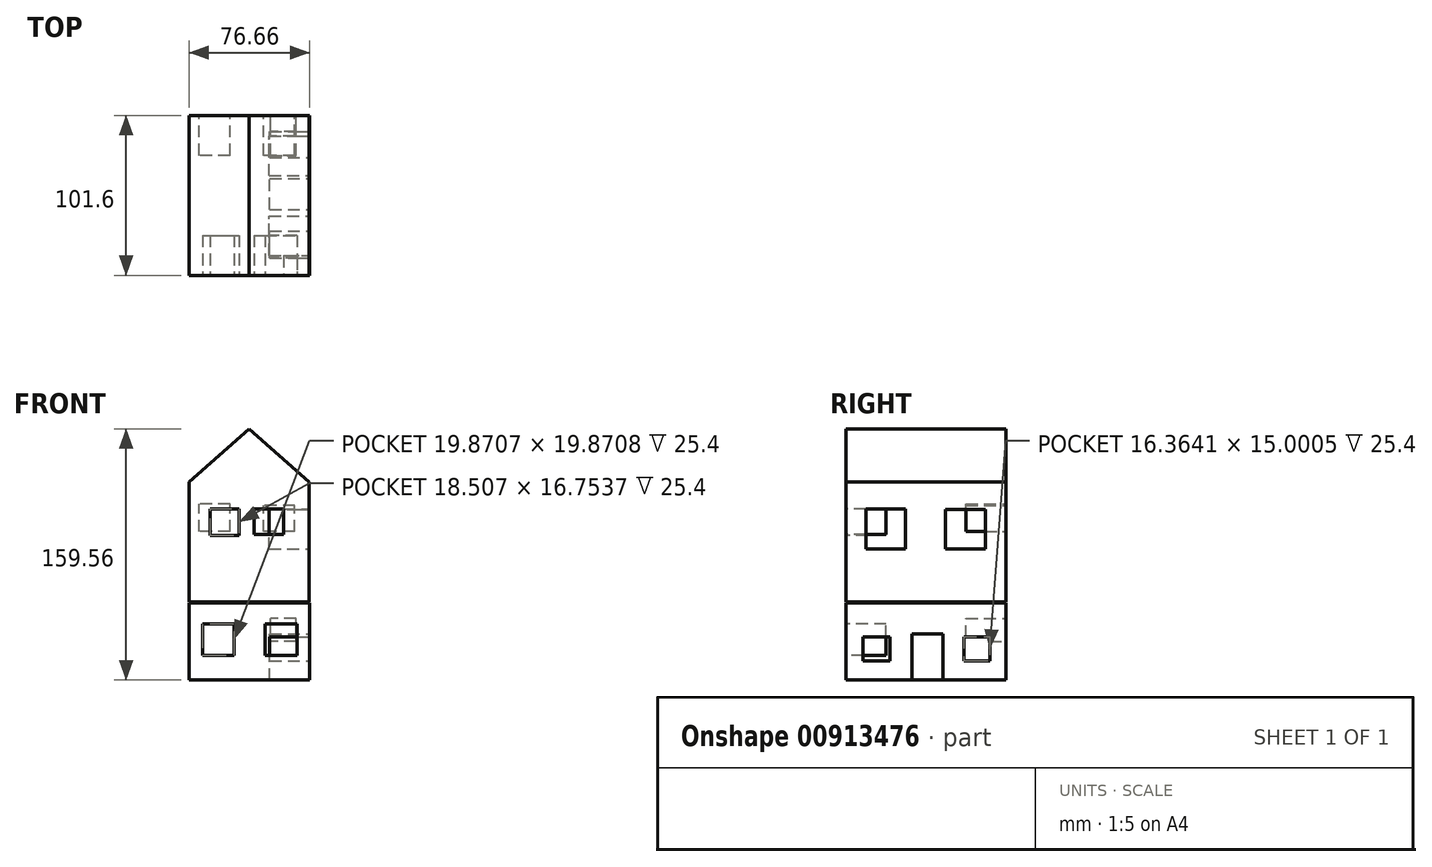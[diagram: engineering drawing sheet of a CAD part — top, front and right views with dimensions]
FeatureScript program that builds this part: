
annotation { "Feature Type Name" : "Feature", "Feature Type Description" : "" }
export const myFeature = defineFeature(function(context is Context, id is Id, definition is map)
    precondition{}
    {
        {
            var Q0;
            Q0=qCreatedBy(makeId("Front.planeOp"),FACE);
            var sketch = newSketch(context, id + "F0", { "sketchPlane" : qUnion([Q0])});
            skLineSegment(sketch, "E0.bottom", {"start": v(-63.36, 87.02) * mm, "end": v(63.64, 87.02) * mm});
            skLineSegment(sketch, "E0.top", {"start": v(-63.36, -39.98) * mm, "end": v(63.64, -39.98) * mm});
            skLineSegment(sketch, "E0.left", {"start": v(-63.36, 87.02) * mm, "end": v(-63.36, -39.98) * mm});
            skLineSegment(sketch, "E0.right", {"start": v(63.64, 87.02) * mm, "end": v(63.64, -39.98) * mm});
            skSolve(sketch);
        }
        {
            var Q0;
            Q0=makeQuery(id+"F0.imprint","IMPRINT",FACE,{"disambiguationData":[TD([[makeQuery(id+"F0.imprint","IMPRINT",EDGE,{"derivedFrom":sQuery(id+"F0.wireOp",EDGE,"E0.bottom")}),-1.0]])]});
            extrude(context, id + "F1", {"entities" : qUnion([Q0]), "depth" : 127 * mm, "offsetDistance" : 25.4 * mm});
        }
        {
            var Q0;
            Q0=makeQuery(id+"F1.opExtrude","CAP_FACE",FACE,{"disambiguationData":[OSD([sQuery(id+"F0.wireOp",EDGE,"E0.bottom"),sQuery(id+"F0.wireOp",EDGE,"E0.top"),sQuery(id+"F0.wireOp",EDGE,"E0.left"),sQuery(id+"F0.wireOp",EDGE,"E0.right")])],"isStart":false});
            extrude(context, id + "F2", {"entities" : qUnion([Q0]), "operationType" : NewBodyOperationType.ADD, "depth" : 76.2 * mm, "offsetDistance" : 25.4 * mm});
        }
        {
            var Q0;
            Q0=makeQuery(id+"F1.opExtrude","SWEPT_BODY",BODY,{"disambiguationData":[OSD([sQuery(id+"F0.wireOp",EDGE,"E0.bottom"),sQuery(id+"F0.wireOp",EDGE,"E0.top"),sQuery(id+"F0.wireOp",EDGE,"E0.left"),sQuery(id+"F0.wireOp",EDGE,"E0.right")])]});
            deleteBodies(context, id + "F3", {"entities" : qUnion([Q0])});
        }
        {
            var Q0;
            Q0=qCreatedBy(makeId("Front.planeOp"),FACE);
            var sketch = newSketch(context, id + "F4", { "sketchPlane" : qUnion([Q0])});
            skLineSegment(sketch, "E1.bottom", {"start": v(-37, 46.06) * mm, "end": v(39.2, 46.06) * mm});
            skLineSegment(sketch, "E1.top", {"start": v(-37, -30.14) * mm, "end": v(39.2, -30.14) * mm});
            skLineSegment(sketch, "E1.left", {"start": v(-37, 46.06) * mm, "end": v(-37, -30.14) * mm});
            skLineSegment(sketch, "E1.right", {"start": v(39.2, 46.06) * mm, "end": v(39.2, -30.14) * mm});
            skSolve(sketch);
        }
        {
            var Q0;
            Q0=makeQuery(id+"F4.imprint","IMPRINT",FACE,{"disambiguationData":[TD([[makeQuery(id+"F4.imprint","IMPRINT",EDGE,{"derivedFrom":sQuery(id+"F4.wireOp",EDGE,"E1.bottom")}),-1.0]])]});
            extrude(context, id + "F5", {"entities" : qUnion([Q0]), "depth" : 76.2 * mm, "offsetDistance" : 25.4 * mm});
        }
        {
            var Q0;
            Q0=makeQuery(id+"F5.opExtrude","SWEPT_BODY",BODY,{"disambiguationData":[OSD([sQuery(id+"F4.wireOp",EDGE,"E1.bottom"),sQuery(id+"F4.wireOp",EDGE,"E1.top"),sQuery(id+"F4.wireOp",EDGE,"E1.left"),sQuery(id+"F4.wireOp",EDGE,"E1.right")])]});
            deleteBodies(context, id + "F6", {"entities" : qUnion([Q0])});
        }
        {
            var Q0;
            Q0=qCreatedBy(makeId("Front.planeOp"),FACE);
            var sketch = newSketch(context, id + "F7", { "sketchPlane" : qUnion([Q0])});
            skLineSegment(sketch, "E2.bottom", {"start": v(-38.1, 42.82) * mm, "end": v(38.1, 42.82) * mm});
            skLineSegment(sketch, "E2.top", {"start": v(-38.1, -33.38) * mm, "end": v(38.1, -33.38) * mm});
            skLineSegment(sketch, "E2.left", {"start": v(-38.1, 42.82) * mm, "end": v(-38.1, -33.38) * mm});
            skLineSegment(sketch, "E2.right", {"start": v(38.1, 42.82) * mm, "end": v(38.1, -33.38) * mm});
            skLineSegment(sketch, "E3", {"start": v(-38.1, 42.82) * mm, "end": v(0, 76.42) * mm});
            skLineSegment(sketch, "E4", {"start": v(38.1, 42.82) * mm, "end": v(0, 76.42) * mm});
            skSolve(sketch);
        }
        {
            var Q0;
            Q0=makeQuery(id+"F7.imprint","IMPRINT",FACE,{"disambiguationData":[TD([[makeQuery(id+"F7.imprint","IMPRINT",EDGE,{"derivedFrom":sQuery(id+"F7.wireOp",EDGE,"E2.bottom")}),1.0]])]});
            var Q1;
            Q1=makeQuery(id+"F7.imprint","IMPRINT",FACE,{"disambiguationData":[TD([[makeQuery(id+"F7.imprint","IMPRINT",EDGE,{"derivedFrom":sQuery(id+"F7.wireOp",EDGE,"E2.bottom")}),-1.0]])]});
            extrude(context, id + "F8", {"entities" : qUnion([Q0, Q1]), "depth" : 101.6 * mm, "offsetDistance" : 25.4 * mm});
        }
        {
            var Q0;
            Q0=qCreatedBy(makeId("Front.planeOp"),FACE);
            var sketch = newSketch(context, id + "F9", { "sketchPlane" : qUnion([Q0])});
            skLineSegment(sketch, "E5.bottom", {"start": v(-38.17, -34.04) * mm, "end": v(38.5, -34.04) * mm});
            skLineSegment(sketch, "E5.top", {"start": v(-38.17, -83.14) * mm, "end": v(38.5, -83.14) * mm});
            skLineSegment(sketch, "E5.left", {"start": v(-38.17, -34.04) * mm, "end": v(-38.17, -83.14) * mm});
            skLineSegment(sketch, "E5.right", {"start": v(38.5, -34.04) * mm, "end": v(38.5, -83.14) * mm});
            skSolve(sketch);
        }
        {
            var Q0;
            Q0 = qSketchRegion(id + "F9", true);
            extrude(context, id + "F10", {"entities" : qUnion([Q0]), "depth" : 101.6 * mm, "offsetDistance" : 25.4 * mm});
        }
        {
            var Q0;
            Q0=makeQuery(id+"F10.opExtrude","SWEPT_FACE",FACE,{"disambiguationData":[OSD([sQuery(id+"F9.wireOp",EDGE,"E5.right")])]});
            var sketch = newSketch(context, id + "F11", { "sketchPlane" : qUnion([Q0])});
            skLineSegment(sketch, "E6", {"start": v(-59.66, -83.14) * mm, "end": v(-59.66, -53.82) * mm});
            skLineSegment(sketch, "E7", {"start": v(-59.66, -53.82) * mm, "end": v(-39.98, -53.82) * mm});
            skLineSegment(sketch, "E8", {"start": v(-39.98, -53.82) * mm, "end": v(-39.98, -83.14) * mm});
            skSolve(sketch);
        }
        {
            var Q0;
            {var subQ0=sQuery(id+"F11.wireOp",EDGE,"E6");Q0=makeQuery(id+"F11.imprint","IMPRINT",FACE,{"disambiguationData":[TD([[makeQuery(id+"F11.imprint","IMPRINT",EDGE,{"derivedFrom":subQ0}),-1.0]])]});}
            extrude(context, id + "F12", {"entities" : qUnion([Q0]), "operationType" : NewBodyOperationType.REMOVE, "oppositeDirection" : true, "depth" : 25.4 * mm, "offsetDistance" : 25.4 * mm});
        }
        {
            var Q0;
            Q0=makeQuery(id+"F8.opExtrude","CAP_FACE",FACE,{"disambiguationData":[OSD([sQuery(id+"F7.wireOp",EDGE,"E2.top"),sQuery(id+"F7.wireOp",EDGE,"E2.left"),sQuery(id+"F7.wireOp",EDGE,"E2.right"),sQuery(id+"F7.wireOp",EDGE,"E3"),sQuery(id+"F7.wireOp",EDGE,"E4")])],"isStart":false});
            var sketch = newSketch(context, id + "F13", { "sketchPlane" : qUnion([Q0])});
            skLineSegment(sketch, "E9.bottom", {"start": v(-24.84, 8.81) * mm, "end": v(-6.33, 8.81) * mm});
            skLineSegment(sketch, "E9.top", {"start": v(-24.84, 25.57) * mm, "end": v(-6.33, 25.57) * mm});
            skLineSegment(sketch, "E9.left", {"start": v(-24.84, 8.81) * mm, "end": v(-24.84, 25.57) * mm});
            skLineSegment(sketch, "E9.right", {"start": v(-6.33, 8.81) * mm, "end": v(-6.33, 25.57) * mm});
            skLineSegment(sketch, "E10.bottom", {"start": v(3.02, 9.4) * mm, "end": v(21.72, 9.4) * mm});
            skLineSegment(sketch, "E10.top", {"start": v(3.02, 25.57) * mm, "end": v(21.72, 25.57) * mm});
            skLineSegment(sketch, "E10.left", {"start": v(3.02, 9.4) * mm, "end": v(3.02, 25.57) * mm});
            skLineSegment(sketch, "E10.right", {"start": v(21.72, 9.4) * mm, "end": v(21.72, 25.57) * mm});
            skSolve(sketch);
        }
        {
            var Q0;
            Q0=makeQuery(id+"F13.imprint","IMPRINT",FACE,{"disambiguationData":[TD([[makeQuery(id+"F13.imprint","IMPRINT",EDGE,{"derivedFrom":sQuery(id+"F13.wireOp",EDGE,"E9.bottom")}),1.0]])]});
            var Q1;
            Q1=makeQuery(id+"F13.imprint","IMPRINT",FACE,{"disambiguationData":[TD([[makeQuery(id+"F13.imprint","IMPRINT",EDGE,{"derivedFrom":sQuery(id+"F13.wireOp",EDGE,"E10.bottom")}),1.0]])]});
            extrude(context, id + "F14", {"entities" : qUnion([Q0, Q1]), "operationType" : NewBodyOperationType.REMOVE, "oppositeDirection" : true, "depth" : 25.4 * mm, "offsetDistance" : 25.4 * mm});
        }
        {
            var Q0;
            Q0=makeQuery(id+"F10.opExtrude","SWEPT_FACE",FACE,{"disambiguationData":[OSD([sQuery(id+"F9.wireOp",EDGE,"E5.right")])]});
            var sketch = newSketch(context, id + "F15", { "sketchPlane" : qUnion([Q0])});
            skLineSegment(sketch, "E11.bottom", {"start": v(-90.72, -70.86) * mm, "end": v(-73.58, -70.86) * mm});
            skLineSegment(sketch, "E11.top", {"start": v(-90.72, -55.86) * mm, "end": v(-73.58, -55.86) * mm});
            skLineSegment(sketch, "E11.left", {"start": v(-90.72, -70.86) * mm, "end": v(-90.72, -55.86) * mm});
            skLineSegment(sketch, "E11.right", {"start": v(-73.58, -70.86) * mm, "end": v(-73.58, -55.86) * mm});
            skLineSegment(sketch, "E12.bottom", {"start": v(-26.63, -70.86) * mm, "end": v(-10.26, -70.86) * mm});
            skLineSegment(sketch, "E12.top", {"start": v(-26.63, -55.86) * mm, "end": v(-10.26, -55.86) * mm});
            skLineSegment(sketch, "E12.left", {"start": v(-26.63, -70.86) * mm, "end": v(-26.63, -55.86) * mm});
            skLineSegment(sketch, "E12.right", {"start": v(-10.26, -70.86) * mm, "end": v(-10.26, -55.86) * mm});
            skSolve(sketch);
        }
        {
            var Q0;
            Q0=makeQuery(id+"F15.imprint","IMPRINT",FACE,{"disambiguationData":[TD([[makeQuery(id+"F15.imprint","IMPRINT",EDGE,{"derivedFrom":sQuery(id+"F15.wireOp",EDGE,"E11.bottom")}),1.0]])]});
            var Q1;
            Q1=makeQuery(id+"F15.imprint","IMPRINT",FACE,{"disambiguationData":[TD([[makeQuery(id+"F15.imprint","IMPRINT",EDGE,{"derivedFrom":sQuery(id+"F15.wireOp",EDGE,"E12.bottom")}),1.0]])]});
            extrude(context, id + "F16", {"entities" : qUnion([Q0, Q1]), "operationType" : NewBodyOperationType.REMOVE, "oppositeDirection" : true, "depth" : 25.4 * mm, "offsetDistance" : 25.4 * mm});
        }
        {
            var Q0;
            Q0=makeQuery(id+"F8.opExtrude","SWEPT_FACE",FACE,{"disambiguationData":[OSD([sQuery(id+"F7.wireOp",EDGE,"E2.right")])]});
            var sketch = newSketch(context, id + "F17", { "sketchPlane" : qUnion([Q0])});
            skLineSegment(sketch, "E13.bottom", {"start": v(-88.97, 0) * mm, "end": v(-64.03, 0) * mm});
            skLineSegment(sketch, "E13.top", {"start": v(-88.97, 25.57) * mm, "end": v(-64.03, 25.57) * mm});
            skLineSegment(sketch, "E13.left", {"start": v(-88.97, 0) * mm, "end": v(-88.97, 25.57) * mm});
            skLineSegment(sketch, "E13.right", {"start": v(-64.03, 0) * mm, "end": v(-64.03, 25.57) * mm});
            skLineSegment(sketch, "E14.bottom", {"start": v(-38.33, 0) * mm, "end": v(-13.2, 0) * mm});
            skLineSegment(sketch, "E14.top", {"start": v(-38.33, 25.4) * mm, "end": v(-13.2, 25.4) * mm});
            skLineSegment(sketch, "E14.left", {"start": v(-38.33, 0) * mm, "end": v(-38.33, 25.4) * mm});
            skLineSegment(sketch, "E14.right", {"start": v(-13.2, 0) * mm, "end": v(-13.2, 25.4) * mm});
            skSolve(sketch);
        }
        {
            var Q0;
            Q0=makeQuery(id+"F17.imprint","IMPRINT",FACE,{"disambiguationData":[TD([[makeQuery(id+"F17.imprint","IMPRINT",EDGE,{"derivedFrom":sQuery(id+"F17.wireOp",EDGE,"E13.bottom")}),1.0]])]});
            var Q1;
            Q1=makeQuery(id+"F17.imprint","IMPRINT",FACE,{"disambiguationData":[TD([[makeQuery(id+"F17.imprint","IMPRINT",EDGE,{"derivedFrom":sQuery(id+"F17.wireOp",EDGE,"E14.bottom")}),1.0]])]});
            extrude(context, id + "F18", {"entities" : qUnion([Q0, Q1]), "operationType" : NewBodyOperationType.REMOVE, "oppositeDirection" : true, "depth" : 25.4 * mm, "offsetDistance" : 25.4 * mm});
        }
        {
            var Q0;
            Q0=makeQuery(id+"F10.opExtrude","CAP_FACE",FACE,{"disambiguationData":[OSD([sQuery(id+"F9.wireOp",EDGE,"E5.bottom"),sQuery(id+"F9.wireOp",EDGE,"E5.top"),sQuery(id+"F9.wireOp",EDGE,"E5.left"),sQuery(id+"F9.wireOp",EDGE,"E5.right")])],"isStart":false});
            var sketch = newSketch(context, id + "F19", { "sketchPlane" : qUnion([Q0])});
            skLineSegment(sketch, "E15.bottom", {"start": v(-29.51, -67.36) * mm, "end": v(-9.64, -67.36) * mm});
            skLineSegment(sketch, "E15.top", {"start": v(-29.51, -47.49) * mm, "end": v(-9.64, -47.49) * mm});
            skLineSegment(sketch, "E15.left", {"start": v(-29.51, -67.36) * mm, "end": v(-29.51, -47.49) * mm});
            skLineSegment(sketch, "E15.right", {"start": v(-9.64, -67.36) * mm, "end": v(-9.64, -47.49) * mm});
            skLineSegment(sketch, "E16.bottom", {"start": v(10.03, -67.36) * mm, "end": v(30.49, -67.36) * mm});
            skLineSegment(sketch, "E16.top", {"start": v(10.03, -47.49) * mm, "end": v(30.49, -47.49) * mm});
            skLineSegment(sketch, "E16.left", {"start": v(10.03, -67.36) * mm, "end": v(10.03, -47.49) * mm});
            skLineSegment(sketch, "E16.right", {"start": v(30.49, -67.36) * mm, "end": v(30.49, -47.49) * mm});
            skSolve(sketch);
        }
        {
            var Q0;
            Q0=makeQuery(id+"F19.imprint","IMPRINT",FACE,{"disambiguationData":[TD([[makeQuery(id+"F19.imprint","IMPRINT",EDGE,{"derivedFrom":sQuery(id+"F19.wireOp",EDGE,"E15.bottom")}),1.0]])]});
            var Q1;
            Q1=makeQuery(id+"F19.imprint","IMPRINT",FACE,{"disambiguationData":[TD([[makeQuery(id+"F19.imprint","IMPRINT",EDGE,{"derivedFrom":sQuery(id+"F19.wireOp",EDGE,"E16.bottom")}),1.0]])]});
            extrude(context, id + "F20", {"entities" : qUnion([Q0, Q1]), "operationType" : NewBodyOperationType.REMOVE, "oppositeDirection" : true, "depth" : 25.4 * mm, "offsetDistance" : 25.4 * mm});
        }
        {
            var Q0;
            Q0=makeQuery(id+"F8.opExtrude","CAP_FACE",FACE,{"disambiguationData":[OSD([sQuery(id+"F7.wireOp",EDGE,"E2.top"),sQuery(id+"F7.wireOp",EDGE,"E2.left"),sQuery(id+"F7.wireOp",EDGE,"E2.right"),sQuery(id+"F7.wireOp",EDGE,"E3"),sQuery(id+"F7.wireOp",EDGE,"E4")])],"isStart":true});
            var sketch = newSketch(context, id + "F21", { "sketchPlane" : qUnion([Q0])});
            skLineSegment(sketch, "E17.bottom", {"start": v(-28.93, 11.15) * mm, "end": v(-9.06, 11.15) * mm});
            skLineSegment(sketch, "E17.top", {"start": v(-28.93, 27.9) * mm, "end": v(-9.06, 27.9) * mm});
            skLineSegment(sketch, "E17.left", {"start": v(-28.93, 11.15) * mm, "end": v(-28.93, 27.9) * mm});
            skLineSegment(sketch, "E17.right", {"start": v(-9.06, 11.15) * mm, "end": v(-9.06, 27.9) * mm});
            skLineSegment(sketch, "E18.bottom", {"start": v(12.18, 11.15) * mm, "end": v(31.66, 11.15) * mm});
            skLineSegment(sketch, "E18.top", {"start": v(12.18, 28.69) * mm, "end": v(31.66, 28.69) * mm});
            skLineSegment(sketch, "E18.left", {"start": v(12.18, 11.15) * mm, "end": v(12.18, 28.69) * mm});
            skLineSegment(sketch, "E18.right", {"start": v(31.66, 11.15) * mm, "end": v(31.66, 28.69) * mm});
            skLineSegment(sketch, "E19.bottom", {"start": v(-26.6, -67.36) * mm, "end": v(-10.62, -67.36) * mm});
            skLineSegment(sketch, "E19.top", {"start": v(-26.6, -49.24) * mm, "end": v(-10.62, -49.24) * mm});
            skLineSegment(sketch, "E19.left", {"start": v(-26.6, -67.36) * mm, "end": v(-26.6, -49.24) * mm});
            skLineSegment(sketch, "E19.right", {"start": v(-10.62, -67.36) * mm, "end": v(-10.62, -49.24) * mm});
            skSolve(sketch);
        }
        {
            var Q0;
            Q0=makeQuery(id+"F21.imprint","IMPRINT",FACE,{"disambiguationData":[TD([[makeQuery(id+"F21.imprint","IMPRINT",EDGE,{"derivedFrom":sQuery(id+"F21.wireOp",EDGE,"E17.bottom")}),1.0]])]});
            var Q1;
            Q1=makeQuery(id+"F21.imprint","IMPRINT",FACE,{"disambiguationData":[TD([[makeQuery(id+"F21.imprint","IMPRINT",EDGE,{"derivedFrom":sQuery(id+"F21.wireOp",EDGE,"E18.bottom")}),1.0]])]});
            extrude(context, id + "F22", {"entities" : qUnion([Q0, Q1]), "operationType" : NewBodyOperationType.REMOVE, "oppositeDirection" : true, "depth" : 25.4 * mm, "offsetDistance" : 25.4 * mm});
        }
        {
            var Q0;
            Q0=makeQuery(id+"F10.opExtrude","CAP_FACE",FACE,{"disambiguationData":[OSD([sQuery(id+"F9.wireOp",EDGE,"E5.bottom"),sQuery(id+"F9.wireOp",EDGE,"E5.top"),sQuery(id+"F9.wireOp",EDGE,"E5.left"),sQuery(id+"F9.wireOp",EDGE,"E5.right")])],"isStart":true});
            var sketch = newSketch(context, id + "F23", { "sketchPlane" : qUnion([Q0])});
            skLineSegment(sketch, "E20.bottom", {"start": v(-29.72, -58.64) * mm, "end": v(-13.54, -58.64) * mm});
            skLineSegment(sketch, "E20.top", {"start": v(-29.72, -44) * mm, "end": v(-13.54, -44) * mm});
            skLineSegment(sketch, "E20.left", {"start": v(-29.72, -58.64) * mm, "end": v(-29.72, -44) * mm});
            skLineSegment(sketch, "E20.right", {"start": v(-13.54, -58.64) * mm, "end": v(-13.54, -44) * mm});
            skSolve(sketch);
        }
        {
            var Q0;
            Q0=makeQuery(id+"F23.imprint","IMPRINT",FACE,{"disambiguationData":[TD([[makeQuery(id+"F23.imprint","IMPRINT",EDGE,{"derivedFrom":sQuery(id+"F23.wireOp",EDGE,"E20.bottom")}),1.0]])]});
            extrude(context, id + "F24", {"entities" : qUnion([Q0]), "operationType" : NewBodyOperationType.REMOVE, "oppositeDirection" : true, "depth" : 25.4 * mm, "offsetDistance" : 25.4 * mm});
        }
    });
